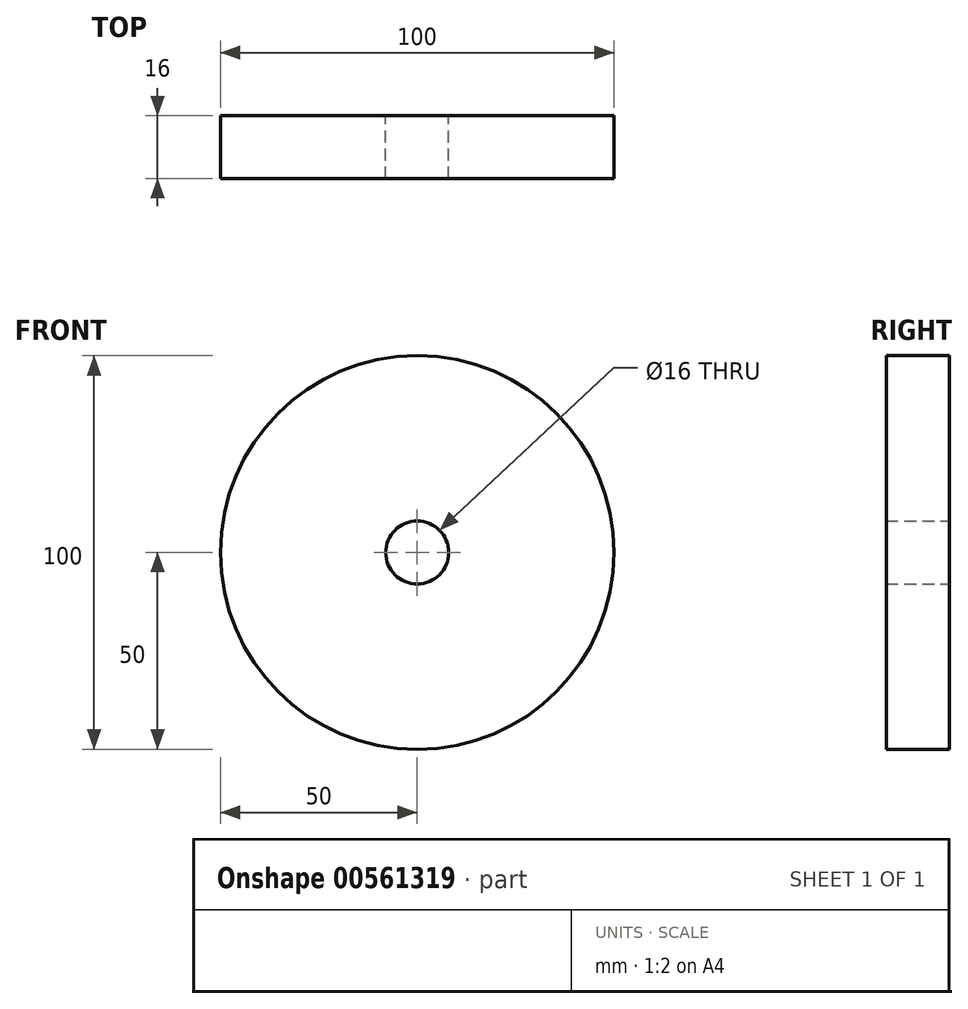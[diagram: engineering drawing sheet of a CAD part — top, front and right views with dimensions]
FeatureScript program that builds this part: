
annotation { "Feature Type Name" : "Feature", "Feature Type Description" : "" }
export const myFeature = defineFeature(function(context is Context, id is Id, definition is map)
    precondition{}
    {
        {
            var Q0;
            Q0=qCreatedBy(makeId("Front.planeOp"),FACE);
            var sketch = newSketch(context, id + "F0", { "sketchPlane" : qUnion([Q0])});
            skCircle(sketch, "E0", {"center": v(0, 0) * mm, "radius": 8 * mm});
            skCircle(sketch, "E1", {"center": v(0, 0) * mm, "radius": 50 * mm});
            skSolve(sketch);
        }
        {
            var Q0;
            Q0 = qSketchRegion(id + "F0", true);
            extrude(context, id + "F1", {"entities" : qUnion([Q0]), "depth" : 16 * mm, "offsetDistance" : 25 * mm});
        }
    });
